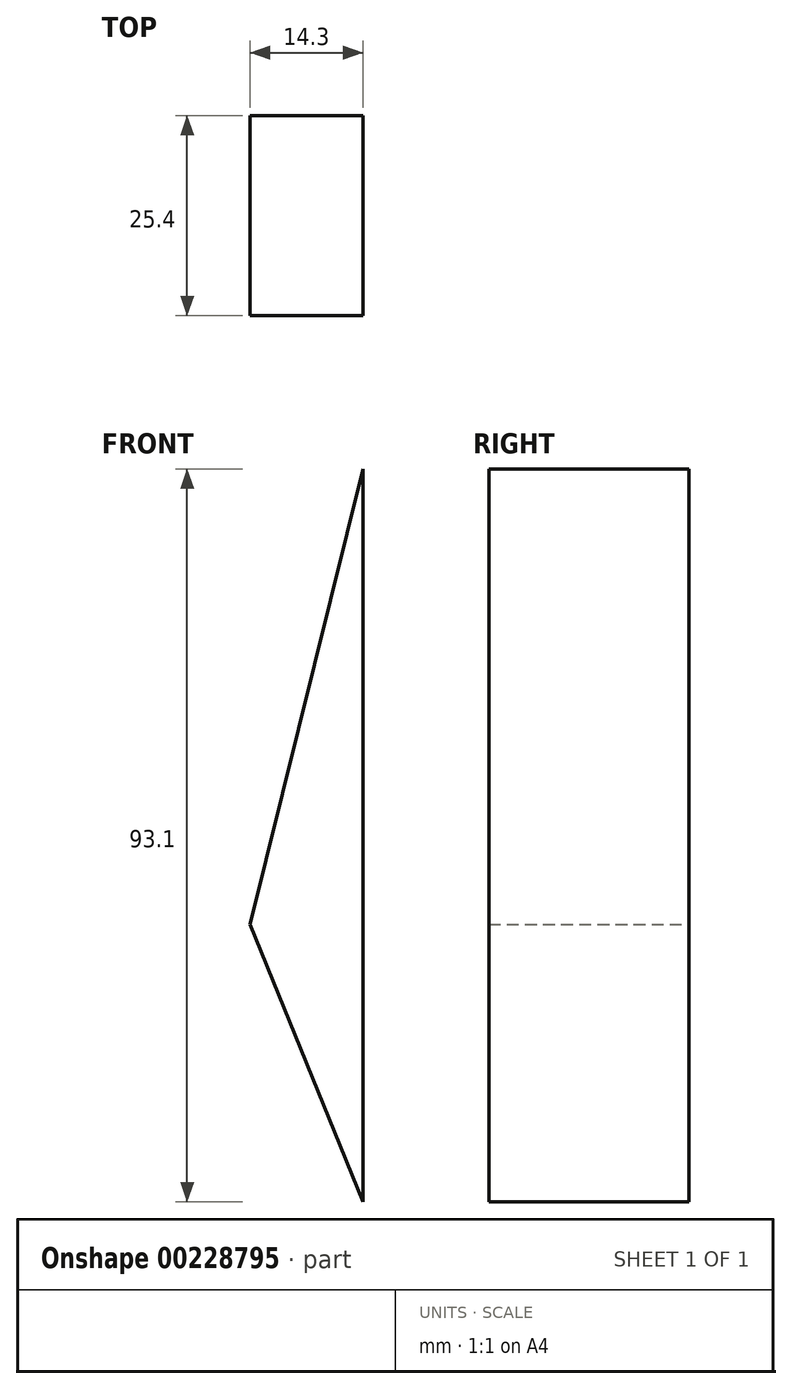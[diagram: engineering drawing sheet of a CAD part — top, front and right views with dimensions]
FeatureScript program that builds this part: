
annotation { "Feature Type Name" : "Feature", "Feature Type Description" : "" }
export const myFeature = defineFeature(function(context is Context, id is Id, definition is map)
    precondition{}
    {
        {
            var Q0;
            Q0=qCreatedBy(makeId("Front.planeOp"),FACE);
            var sketch = newSketch(context, id + "F0", { "sketchPlane" : qUnion([Q0])});
            skLineSegment(sketch, "E0", {"start": v(0, 57.85) * mm, "end": v(-14.3, 0) * mm});
            skLineSegment(sketch, "E1", {"start": v(-14.3, 0) * mm, "end": v(0, -35.25) * mm});
            skLineSegment(sketch, "E2", {"start": v(0, -35.25) * mm, "end": v(0, 57.85) * mm});
            skSolve(sketch);
        }
        {
            var Q0;
            Q0 = qSketchRegion(id + "F0", true);
            extrude(context, id + "F1", {"entities" : qUnion([Q0]), "depth" : 25.4 * mm});
        }
    });
